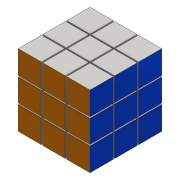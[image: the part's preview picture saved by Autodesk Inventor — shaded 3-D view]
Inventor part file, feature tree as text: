
AUTODESK INVENTOR PART (.ipt)
format: ipt  version: 2016 (Build 200138000, 138)  size: 330,240 bytes
history: native  units: mm
features: extrude x6, sketch x6, mirror x4, plane x3, pattern_circular x3, projected_geometry x1
ambient origin geometry x8: Origin, YZ Plane, XZ Plane, XY Plane, X Axis, Y Axis, Z Axis, Center Point
bodies: 实体1 (feature_tree)
feature tree (23):
  extrude  "拉伸1"  Depth=57.0mm TaperAngle=0.0deg
  extrude  "拉伸2"  Depth=1.0mm
  mirror  "镜像1"
  extrude  "拉伸3"  Depth=18.5mm
  plane  "工作平面1"
  mirror  "镜像2"
  pattern_circular  "环形阵列1"  Count=4 Angle=360.0deg
  pattern_circular  "环形阵列2"  Count=4 Angle=360.0deg
  extrude  "拉伸4"  Depth=1.0mm TaperAngle=0.0deg
  pattern_circular  "环形阵列3"  Count=4 Angle=360.0deg
  extrude  "拉伸5"  Depth=1.0mm
  mirror  "镜像3"
  extrude  "拉伸6"  Depth=18.5mm
  mirror  "镜像4"
  sketch  "草图1"  dims[d0=57.0mm d1=57.0mm d2=0.0mm]
  sketch  "草图2"  dims[d3=18.5mm d4=1.0mm]
  projected_geometry  "投影回路1"
  sketch  "草图3"  dims[d5=1.0mm d6=18.5mm]
  sketch  "草图4"  dims[d7=1.0mm d8=0.0mm]
  sketch  "草图5"  dims[d9=1.0mm d10=0.0mm]
  plane  "工作平面2"
  sketch  "草图6"  dims[d11=28.5mm d12=40.0mm d13=360.0deg d15=40.0mm d16=360.0deg d18=1.0mm d19=0.0mm d20=40.0mm d21=360.0deg d23=1.0mm d24=18.5mm d25=1.0mm d26=18.5mm d27=60.0mm d28=0.0mm d29=1.0mm d30=0.0mm]
  plane  "工作平面3"
